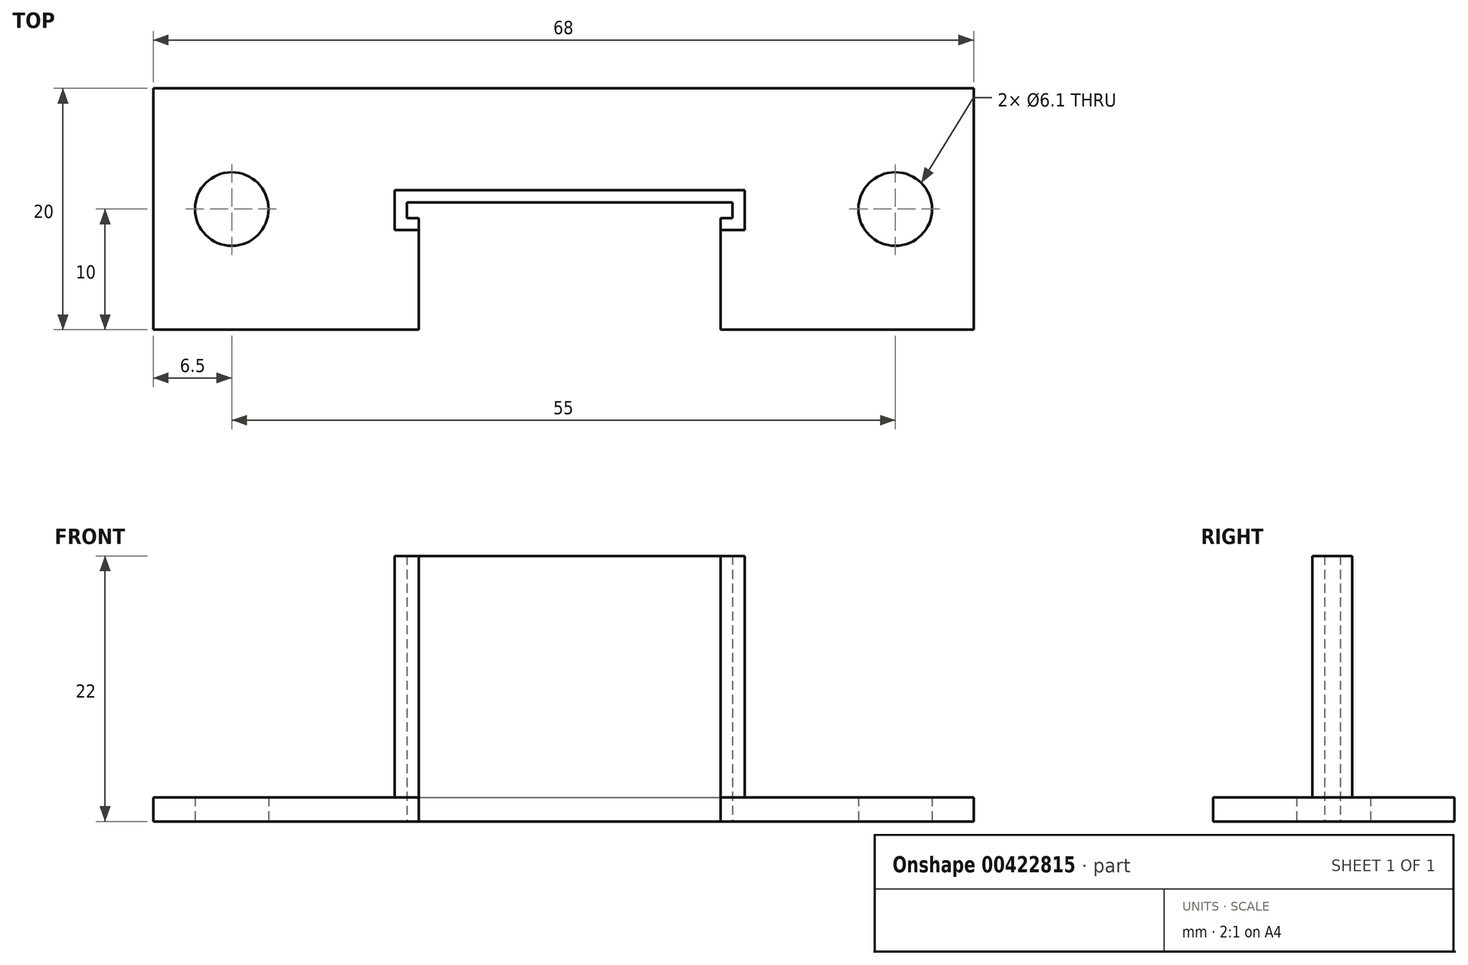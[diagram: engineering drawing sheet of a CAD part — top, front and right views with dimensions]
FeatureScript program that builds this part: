
annotation { "Feature Type Name" : "Feature", "Feature Type Description" : "" }
export const myFeature = defineFeature(function(context is Context, id is Id, definition is map)
    precondition{}
    {
        {
            var Q0;
            Q0=qCreatedBy(makeId("Top.planeOp"),FACE);
            var sketch = newSketch(context, id + "F0", { "sketchPlane" : qUnion([Q0])});
            skLineSegment(sketch, "E0.bottom", {"start": v(0, 0) * mm, "end": v(80, 0) * mm});
            skLineSegment(sketch, "E0.top", {"start": v(0, 20) * mm, "end": v(80, 20) * mm});
            skLineSegment(sketch, "E0.left", {"start": v(0, 0) * mm, "end": v(0, 20) * mm});
            skLineSegment(sketch, "E0.right", {"start": v(80, 0) * mm, "end": v(80, 20) * mm});
            skLineSegment(sketch, "E1.bottom", {"start": v(27, 10.55) * mm, "end": v(54, 10.55) * mm});
            skLineSegment(sketch, "E1.top", {"start": v(27, 9.25) * mm, "end": v(54, 9.25) * mm});
            skLineSegment(sketch, "E1.left", {"start": v(27, 10.55) * mm, "end": v(27, 9.25) * mm});
            skLineSegment(sketch, "E1.right", {"start": v(54, 10.55) * mm, "end": v(54, 9.25) * mm});
            skPoint(sketch, "E2", {"position": v(0, 10) * mm});
            skPoint(sketch, "E3", {"position": v(12.5, 10) * mm});
            skPoint(sketch, "E4", {"position": v(67.5, 10) * mm});
            skPoint(sketch, "E4.positionSnap0", {"position": v(80, 10) * mm});
            skCircle(sketch, "E5", {"center": v(12.5, 10) * mm, "radius": 3.05 * mm});
            skCircle(sketch, "E6", {"center": v(67.5, 10) * mm, "radius": 3.05 * mm});
            skLineSegment(sketch, "E7.bottom", {"start": v(28, 0) * mm, "end": v(53, 0) * mm});
            skLineSegment(sketch, "E7.top", {"start": v(28, 9.25) * mm, "end": v(53, 9.25) * mm});
            skLineSegment(sketch, "E7.left", {"start": v(28, 0) * mm, "end": v(28, 9.25) * mm});
            skLineSegment(sketch, "E7.right", {"start": v(53, 0) * mm, "end": v(53, 9.25) * mm});
            skLineSegment(sketch, "E8.bottom", {"start": v(6, 20) * mm, "end": v(74, 20) * mm});
            skLineSegment(sketch, "E8.top", {"start": v(6, 0) * mm, "end": v(74, 0) * mm});
            skLineSegment(sketch, "E8.left", {"start": v(6, 20) * mm, "end": v(6, 0) * mm});
            skLineSegment(sketch, "E8.right", {"start": v(74, 20) * mm, "end": v(74, 0) * mm});
            skSolve(sketch);
        }
        {
            var Q0;
            Q0=makeQuery(id+"F0.imprint","IMPRINT",FACE,{"disambiguationData":[TD([[makeQuery(id+"F0.imprint","IMPRINT",EDGE,{"derivedFrom":sQuery(id+"F0.wireOp",EDGE,"E1.bottom")}),1.0]])]});
            extrude(context, id + "F1", {"entities" : qUnion([Q0]), "depth" : 2 * mm});
        }
        {
            var Q0;
            Q0=makeQuery(id+"F1.opExtrude","CAP_FACE",FACE,{"disambiguationData":[OSD([sQuery(id+"F0.wireOp",EDGE,"E0.bottom"),sQuery(id+"F0.wireOp",EDGE,"E0.top"),sQuery(id+"F0.wireOp",EDGE,"E0.left"),sQuery(id+"F0.wireOp",EDGE,"E0.right"),sQuery(id+"F0.wireOp",EDGE,"E1.bottom"),sQuery(id+"F0.wireOp",EDGE,"E1.top"),sQuery(id+"F0.wireOp",EDGE,"E1.left"),sQuery(id+"F0.wireOp",EDGE,"E1.right"),sQuery(id+"F0.wireOp",EDGE,"E5"),sQuery(id+"F0.wireOp",EDGE,"E6")])],"isStart":false});
            var sketch = newSketch(context, id + "F2", { "sketchPlane" : qUnion([Q0])});
            skLineSegment(sketch, "E9.bottom", {"start": v(27, 10.55) * mm, "end": v(54, 10.55) * mm});
            skLineSegment(sketch, "E9.top", {"start": v(27, 11.55) * mm, "end": v(54, 11.55) * mm});
            skLineSegment(sketch, "E9.left", {"start": v(27, 10.55) * mm, "end": v(27, 11.55) * mm});
            skLineSegment(sketch, "E9.right", {"start": v(54, 10.55) * mm, "end": v(54, 11.55) * mm});
            skLineSegment(sketch, "E10.bottom", {"start": v(54, 11.55) * mm, "end": v(54, 11.55) * mm});
            skLineSegment(sketch, "E10.top", {"start": v(54, 9.25) * mm, "end": v(54, 9.25) * mm});
            skLineSegment(sketch, "E10.left", {"start": v(54, 11.55) * mm, "end": v(54, 9.25) * mm});
            skLineSegment(sketch, "E10.right", {"start": v(54, 11.55) * mm, "end": v(54, 9.25) * mm});
            skLineSegment(sketch, "E11.bottom", {"start": v(55, 9.25) * mm, "end": v(54, 9.25) * mm});
            skLineSegment(sketch, "E11.top", {"start": v(55, 11.55) * mm, "end": v(54, 11.55) * mm});
            skLineSegment(sketch, "E11.left", {"start": v(55, 9.25) * mm, "end": v(55, 11.55) * mm});
            skLineSegment(sketch, "E11.right", {"start": v(54, 9.25) * mm, "end": v(54, 11.55) * mm});
            skLineSegment(sketch, "E12.bottom", {"start": v(27, 11.55) * mm, "end": v(27, 11.55) * mm});
            skLineSegment(sketch, "E12.top", {"start": v(27, 9.25) * mm, "end": v(27, 9.25) * mm});
            skLineSegment(sketch, "E12.left", {"start": v(27, 11.55) * mm, "end": v(27, 9.25) * mm});
            skLineSegment(sketch, "E12.right", {"start": v(27, 11.55) * mm, "end": v(27, 9.25) * mm});
            skLineSegment(sketch, "E13.bottom", {"start": v(27, 9.25) * mm, "end": v(26, 9.25) * mm});
            skLineSegment(sketch, "E13.top", {"start": v(27, 11.55) * mm, "end": v(26, 11.55) * mm});
            skLineSegment(sketch, "E13.left", {"start": v(27, 9.25) * mm, "end": v(27, 11.55) * mm});
            skLineSegment(sketch, "E13.right", {"start": v(26, 9.25) * mm, "end": v(26, 11.55) * mm});
            skLineSegment(sketch, "E14.bottom", {"start": v(26, 9.25) * mm, "end": v(28, 9.25) * mm});
            skLineSegment(sketch, "E14.top", {"start": v(26, 8.25) * mm, "end": v(28, 8.25) * mm});
            skLineSegment(sketch, "E14.left", {"start": v(26, 9.25) * mm, "end": v(26, 8.25) * mm});
            skLineSegment(sketch, "E14.right", {"start": v(28, 9.25) * mm, "end": v(28, 8.25) * mm});
            skLineSegment(sketch, "E15.bottom", {"start": v(55, 9.25) * mm, "end": v(53, 9.25) * mm});
            skLineSegment(sketch, "E15.top", {"start": v(55, 8.25) * mm, "end": v(53, 8.25) * mm});
            skLineSegment(sketch, "E15.left", {"start": v(55, 9.25) * mm, "end": v(55, 8.25) * mm});
            skLineSegment(sketch, "E15.right", {"start": v(53, 9.25) * mm, "end": v(53, 8.25) * mm});
            skSolve(sketch);
        }
        {
            var Q0;
            Q0 = qSketchRegion(id + "F2", true);
            extrude(context, id + "F3", {"entities" : qUnion([Q0]), "operationType" : NewBodyOperationType.ADD, "depth" : 20 * mm});
        }
    });
